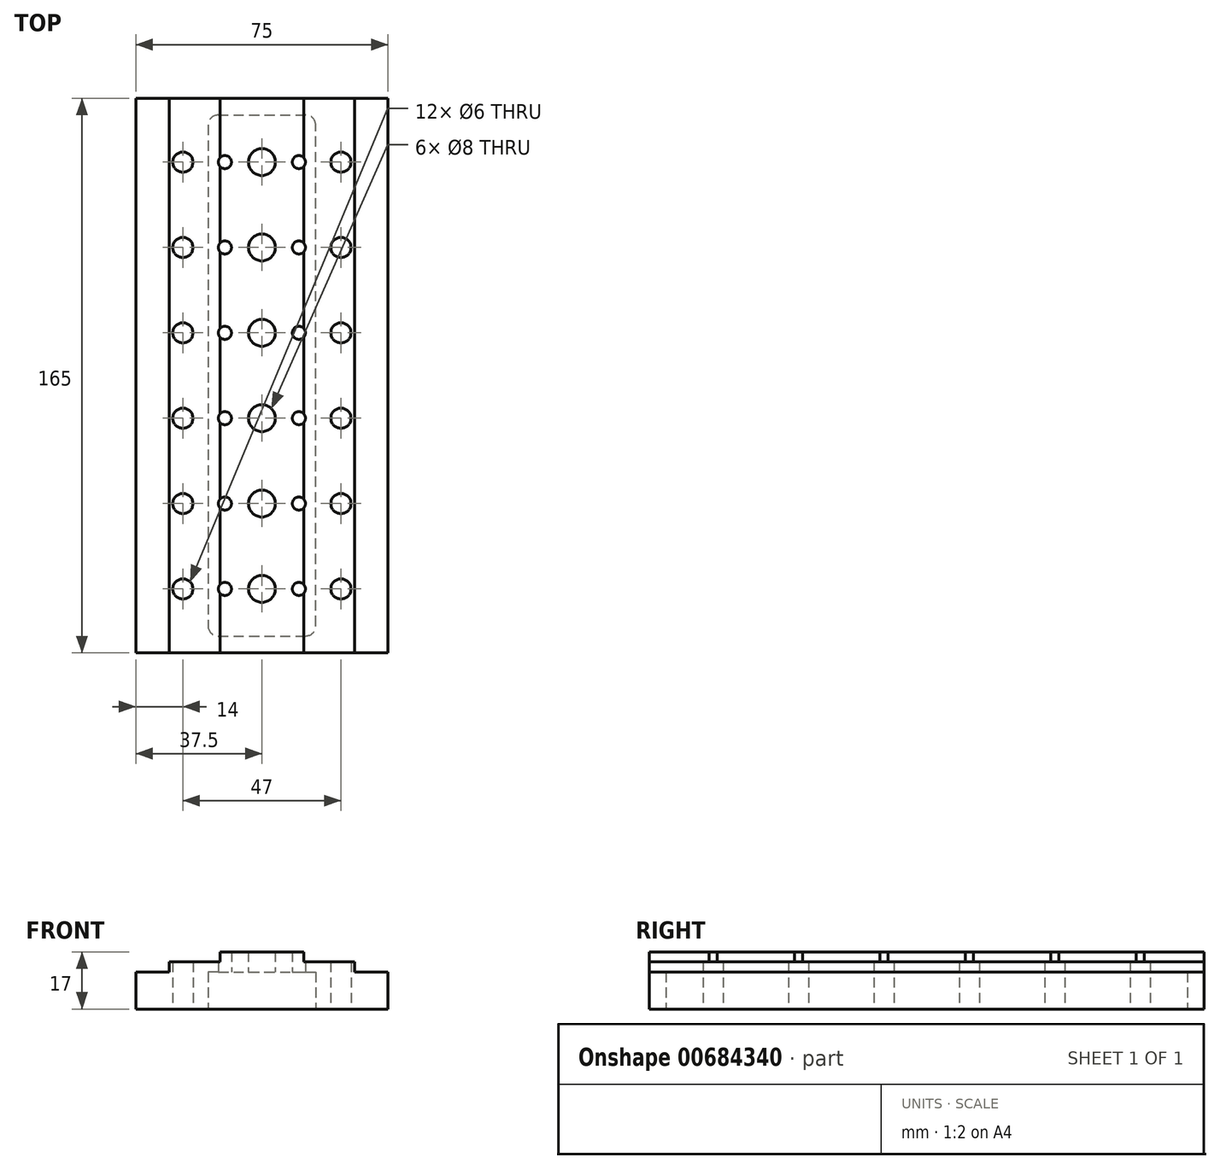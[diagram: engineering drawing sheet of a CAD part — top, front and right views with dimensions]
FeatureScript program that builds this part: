
annotation { "Feature Type Name" : "Feature", "Feature Type Description" : "" }
export const myFeature = defineFeature(function(context is Context, id is Id, definition is map)
    precondition{}
    {
        {
            var Q0;
            Q0=qCreatedBy(makeId("Front.planeOp"),FACE);
            var sketch = newSketch(context, id + "F0", { "sketchPlane" : qUnion([Q0])});
            skLineSegment(sketch, "E0", {"start": v(0, 0) * mm, "end": v(75, 0) * mm});
            skLineSegment(sketch, "E1", {"start": v(75, 14) * mm, "end": v(75, 0) * mm});
            skLineSegment(sketch, "E2", {"start": v(75, 14) * mm, "end": v(50, 14) * mm});
            skLineSegment(sketch, "E3", {"start": v(50, 14) * mm, "end": v(50, 17) * mm});
            skLineSegment(sketch, "E4", {"start": v(50, 17) * mm, "end": v(25, 17) * mm});
            skLineSegment(sketch, "E5", {"start": v(25, 17) * mm, "end": v(25, 14) * mm});
            skLineSegment(sketch, "E6", {"start": v(25, 14) * mm, "end": v(0, 14) * mm});
            skLineSegment(sketch, "E7", {"start": v(0, 14) * mm, "end": v(0, 0) * mm});
            skSolve(sketch);
        }
        {
            var Q0;
            Q0=makeQuery(id+"F0.imprint","IMPRINT",FACE,{"disambiguationData":[TD([[makeQuery(id+"F0.imprint","IMPRINT",EDGE,{"derivedFrom":sQuery(id+"F0.wireOp",EDGE,"E0")}),1.0]])]});
            extrude(context, id + "F1", {"entities" : qUnion([Q0]), "depth" : 165 * mm, "offsetDistance" : 25 * mm});
        }
        {
            var Q0;
            Q0=makeQuery(id+"F1.opExtrude","SWEPT_FACE",FACE,{"disambiguationData":[OSD([sQuery(id+"F0.wireOp",EDGE,"E0")])]});
            var sketch = newSketch(context, id + "F2", { "sketchPlane" : qUnion([Q0])});
            skPoint(sketch, "E8", {"position": v(14, 146) * mm});
            skPoint(sketch, "E9", {"position": v(37.5, 146) * mm});
            skPoint(sketch, "E9.positionSnap0", {"position": v(37.5, 165) * mm});
            skPoint(sketch, "E10", {"position": v(61, 146) * mm});
            skPoint(sketch, "E11", {"position": v(14, 120.6) * mm});
            skPoint(sketch, "E12", {"position": v(14, 95.2) * mm});
            skPoint(sketch, "E13", {"position": v(14, 69.8) * mm});
            skPoint(sketch, "E14", {"position": v(14, 44.4) * mm});
            skPoint(sketch, "E15", {"position": v(14, 19) * mm});
            skPoint(sketch, "E16", {"position": v(37.5, 120.6) * mm});
            skPoint(sketch, "E17", {"position": v(37.5, 95.2) * mm});
            skPoint(sketch, "E18", {"position": v(37.5, 69.8) * mm});
            skPoint(sketch, "E19", {"position": v(37.5, 44.4) * mm});
            skPoint(sketch, "E20", {"position": v(37.5, 19) * mm});
            skPoint(sketch, "E21", {"position": v(61, 120.6) * mm});
            skPoint(sketch, "E22", {"position": v(61, 95.2) * mm});
            skPoint(sketch, "E23", {"position": v(61, 69.8) * mm});
            skPoint(sketch, "E24", {"position": v(61, 44.4) * mm});
            skPoint(sketch, "E25", {"position": v(61, 19) * mm});
            skPoint(sketch, "E26", {"position": v(26.5, 146) * mm});
            skPoint(sketch, "E27", {"position": v(26.5, 120.6) * mm});
            skPoint(sketch, "E28", {"position": v(26.5, 95.2) * mm});
            skPoint(sketch, "E29", {"position": v(26.5, 69.8) * mm});
            skPoint(sketch, "E30", {"position": v(26.5, 44.4) * mm});
            skPoint(sketch, "E31", {"position": v(26.5, 19) * mm});
            skPoint(sketch, "E32", {"position": v(48.5, 146) * mm});
            skPoint(sketch, "E33", {"position": v(48.5, 120.6) * mm});
            skPoint(sketch, "E34", {"position": v(48.5, 95.2) * mm});
            skPoint(sketch, "E35", {"position": v(48.5, 69.8) * mm});
            skPoint(sketch, "E36", {"position": v(48.5, 44.4) * mm});
            skPoint(sketch, "E37", {"position": v(48.5, 19) * mm});
            skSolve(sketch);
        }
        {
            var Q0;
            Q0=sQuery(id+"F2.wireOp",VERTEX,"E8");
            var Q1;
            Q1=sQuery(id+"F2.wireOp",VERTEX,"E11");
            var Q2;
            Q2=sQuery(id+"F2.wireOp",VERTEX,"E12");
            var Q3;
            Q3=sQuery(id+"F2.wireOp",VERTEX,"E13");
            var Q4;
            Q4=sQuery(id+"F2.wireOp",VERTEX,"E14");
            var Q5;
            Q5=sQuery(id+"F2.wireOp",VERTEX,"E15");
            var Q6;
            Q6=sQuery(id+"F2.wireOp",VERTEX,"E10");
            var Q7;
            Q7=sQuery(id+"F2.wireOp",VERTEX,"E21");
            var Q8;
            Q8=sQuery(id+"F2.wireOp",VERTEX,"E22");
            var Q9;
            Q9=sQuery(id+"F2.wireOp",VERTEX,"E23");
            var Q10;
            Q10=sQuery(id+"F2.wireOp",VERTEX,"E24");
            var Q11;
            Q11=sQuery(id+"F2.wireOp",VERTEX,"E25");
            var Q12;
            Q12=makeQuery(id+"F1.opExtrude","SWEPT_BODY",BODY,{"disambiguationData":[OSD([sQuery(id+"F0.wireOp",EDGE,"E0"),sQuery(id+"F0.wireOp",EDGE,"E1"),sQuery(id+"F0.wireOp",EDGE,"E2"),sQuery(id+"F0.wireOp",EDGE,"E3"),sQuery(id+"F0.wireOp",EDGE,"E4"),sQuery(id+"F0.wireOp",EDGE,"E5"),sQuery(id+"F0.wireOp",EDGE,"E6"),sQuery(id+"F0.wireOp",EDGE,"E7")])]});
            hole(context, id + "F3", {"style" : HoleStyle.SIMPLE, "endStyle" : HoleEndStyle.THROUGH, "standardTappedOrClearance" : lookupTablePath({ "standard" : "ISO", "size" : "6", "type" : "Drilled" }), "standardBlindInLast" : lookupTablePath({ "standard" : "ISO", "size" : "6", "type" : "Drilled" }), "holeDiameter" : 6 * mm, "majorDiameter" : 5 * mm, "isTappedThrough" : true, "tappedDepth" : 17.25 * mm, "tapClearance" : 3, "startFromSketch" : true, "locations" : qUnion([Q0, Q1, Q2, Q3, Q4, Q5, Q6, Q7, Q8, Q9, Q10, Q11]), "scope" : qUnion([Q12])});
        }
        {
            var Q0;
            Q0=sQuery(id+"F2.wireOp",VERTEX,"E26");
            var Q1;
            Q1=sQuery(id+"F2.wireOp",VERTEX,"E27");
            var Q2;
            Q2=sQuery(id+"F2.wireOp",VERTEX,"E28");
            var Q3;
            Q3=sQuery(id+"F2.wireOp",VERTEX,"E29");
            var Q4;
            Q4=sQuery(id+"F2.wireOp",VERTEX,"E30");
            var Q5;
            Q5=sQuery(id+"F2.wireOp",VERTEX,"E31");
            var Q6;
            Q6=sQuery(id+"F2.wireOp",VERTEX,"E37");
            var Q7;
            Q7=sQuery(id+"F2.wireOp",VERTEX,"E36");
            var Q8;
            Q8=sQuery(id+"F2.wireOp",VERTEX,"E35");
            var Q9;
            Q9=sQuery(id+"F2.wireOp",VERTEX,"E34");
            var Q10;
            Q10=sQuery(id+"F2.wireOp",VERTEX,"E33");
            var Q11;
            Q11=sQuery(id+"F2.wireOp",VERTEX,"E32");
            var Q12;
            Q12=makeQuery(id+"F1.opExtrude","SWEPT_BODY",BODY,{"disambiguationData":[OSD([sQuery(id+"F0.wireOp",EDGE,"E0"),sQuery(id+"F0.wireOp",EDGE,"E1"),sQuery(id+"F0.wireOp",EDGE,"E2"),sQuery(id+"F0.wireOp",EDGE,"E3"),sQuery(id+"F0.wireOp",EDGE,"E4"),sQuery(id+"F0.wireOp",EDGE,"E5"),sQuery(id+"F0.wireOp",EDGE,"E6"),sQuery(id+"F0.wireOp",EDGE,"E7")])]});
            hole(context, id + "F4", {"style" : HoleStyle.SIMPLE, "endStyle" : HoleEndStyle.THROUGH, "standardTappedOrClearance" : lookupTablePath({ "standard" : "ISO", "size" : "3.9", "type" : "Drilled" }), "standardBlindInLast" : lookupTablePath({ "standard" : "ISO", "size" : "3.9", "type" : "Drilled" }), "holeDiameter" : 3.9 * mm, "majorDiameter" : 5 * mm, "isTappedThrough" : true, "tappedDepth" : 17.25 * mm, "tapClearance" : 3, "startFromSketch" : true, "locations" : qUnion([Q0, Q1, Q2, Q3, Q4, Q5, Q6, Q7, Q8, Q9, Q10, Q11]), "scope" : qUnion([Q12])});
        }
        {
            var Q0;
            Q0=sQuery(id+"F2.wireOp",VERTEX,"E9");
            var Q1;
            Q1=sQuery(id+"F2.wireOp",VERTEX,"E16");
            var Q2;
            Q2=sQuery(id+"F2.wireOp",VERTEX,"E17");
            var Q3;
            Q3=sQuery(id+"F2.wireOp",VERTEX,"E18");
            var Q4;
            Q4=sQuery(id+"F2.wireOp",VERTEX,"E19");
            var Q5;
            Q5=sQuery(id+"F2.wireOp",VERTEX,"E20");
            var Q6;
            Q6=makeQuery(id+"F1.opExtrude","SWEPT_BODY",BODY,{"disambiguationData":[OSD([sQuery(id+"F0.wireOp",EDGE,"E0"),sQuery(id+"F0.wireOp",EDGE,"E1"),sQuery(id+"F0.wireOp",EDGE,"E2"),sQuery(id+"F0.wireOp",EDGE,"E3"),sQuery(id+"F0.wireOp",EDGE,"E4"),sQuery(id+"F0.wireOp",EDGE,"E5"),sQuery(id+"F0.wireOp",EDGE,"E6"),sQuery(id+"F0.wireOp",EDGE,"E7")])]});
            hole(context, id + "F5", {"style" : HoleStyle.SIMPLE, "endStyle" : HoleEndStyle.THROUGH, "standardTappedOrClearance" : lookupTablePath({ "standard" : "ISO", "size" : "8", "type" : "Drilled" }), "standardBlindInLast" : lookupTablePath({ "standard" : "ISO", "size" : "8", "type" : "Drilled" }), "holeDiameter" : 8 * mm, "majorDiameter" : 5 * mm, "isTappedThrough" : true, "tappedDepth" : 17.25 * mm, "tapClearance" : 3, "startFromSketch" : true, "locations" : qUnion([Q0, Q1, Q2, Q3, Q4, Q5]), "scope" : qUnion([Q6])});
        }
        {
            var Q0;
            {var subQ0=sQuery(id+"F0.wireOp",EDGE,"E0");Q0=makeQuery(id+"F2.imprint","IMPRINT",FACE,{"disambiguationData":[TD([[makeQuery(id+"F2.imprint","IMPRINT",EDGE,{"derivedFrom":makeQuery(id+"F1.opExtrude","CAP_EDGE",EDGE,{"disambiguationData":[OSD([subQ0])],"isStart":true})}),1.0]])]});}
            var sketch = newSketch(context, id + "F6", { "sketchPlane" : qUnion([Q0])});
            skLineSegment(sketch, "E38", {"start": v(21.5, 160) * mm, "end": v(53.5, 160) * mm});
            skLineSegment(sketch, "E39", {"start": v(53.5, 160) * mm, "end": v(53.5, 5) * mm});
            skLineSegment(sketch, "E40", {"start": v(21.5, 5) * mm, "end": v(53.5, 5) * mm});
            skLineSegment(sketch, "E41", {"start": v(21.5, 5) * mm, "end": v(21.5, 160) * mm});
            skSolve(sketch);
        }
        {
            var Q0;
            Q0=makeQuery(id+"F6.imprint","IMPRINT",FACE,{"disambiguationData":[TD([[makeQuery(id+"F6.imprint","IMPRINT",EDGE,{"derivedFrom":sQuery(id+"F6.wireOp",EDGE,"E38")}),-1.0]])]});
            extrude(context, id + "F7", {"entities" : qUnion([Q0]), "operationType" : NewBodyOperationType.REMOVE, "oppositeDirection" : true, "depth" : 11 * mm, "offsetDistance" : 25 * mm});
        }
        {
            var Q0;
            Q0=makeQuery(id+"F7.boolean.opBoolean","COPY",EDGE,{"derivedFrom":makeQuery(id+"F7.opExtrude","SWEPT_EDGE",EDGE,{"disambiguationData":[OSD([sQuery(id+"F6.wireOp",EDGE,"E38"),sQuery(id+"F6.wireOp",EDGE,"E41")])]})});
            var Q1;
            Q1=makeQuery(id+"F7.boolean.opBoolean","COPY",EDGE,{"derivedFrom":makeQuery(id+"F7.opExtrude","SWEPT_EDGE",EDGE,{"disambiguationData":[OSD([sQuery(id+"F6.wireOp",EDGE,"E38"),sQuery(id+"F6.wireOp",EDGE,"E39")])]})});
            var Q2;
            Q2=makeQuery(id+"F7.boolean.opBoolean","COPY",EDGE,{"derivedFrom":makeQuery(id+"F7.opExtrude","SWEPT_EDGE",EDGE,{"disambiguationData":[OSD([sQuery(id+"F6.wireOp",EDGE,"E40"),sQuery(id+"F6.wireOp",EDGE,"E41")])]})});
            var Q3;
            Q3=makeQuery(id+"F7.boolean.opBoolean","COPY",EDGE,{"derivedFrom":makeQuery(id+"F7.opExtrude","SWEPT_EDGE",EDGE,{"disambiguationData":[OSD([sQuery(id+"F6.wireOp",EDGE,"E39"),sQuery(id+"F6.wireOp",EDGE,"E40")])]})});
            fillet(context, id + "F8", {"entities" : qUnion([Q0, Q1, Q2, Q3]), "radius" : 3 * mm, "tangentPropagation" : true, "allowEdgeOverflow" : false});
        }
        {
            var Q0;
            Q0=makeQuery(id+"F1.opExtrude","SWEPT_FACE",FACE,{"disambiguationData":[OSD([sQuery(id+"F0.wireOp",EDGE,"E2")])]});
            var sketch = newSketch(context, id + "F9", { "sketchPlane" : qUnion([Q0])});
            skLineSegment(sketch, "E42", {"start": v(65, 0) * mm, "end": v(65, -165) * mm});
            skLineSegment(sketch, "E43", {"start": v(65, -165) * mm, "end": v(75, -165) * mm});
            skLineSegment(sketch, "E44", {"start": v(75, -165) * mm, "end": v(75, 0) * mm});
            skLineSegment(sketch, "E45", {"start": v(75, 0) * mm, "end": v(65, 0) * mm});
            skSolve(sketch);
        }
        {
            var Q0;
            Q0=makeQuery(id+"F1.opExtrude","SWEPT_FACE",FACE,{"disambiguationData":[OSD([sQuery(id+"F0.wireOp",EDGE,"E6")])]});
            var sketch = newSketch(context, id + "F10", { "sketchPlane" : qUnion([Q0])});
            skLineSegment(sketch, "E46", {"start": v(10, 0) * mm, "end": v(10, -165) * mm});
            skLineSegment(sketch, "E47", {"start": v(10, -165) * mm, "end": v(0, -165) * mm});
            skLineSegment(sketch, "E48", {"start": v(0, -165) * mm, "end": v(0, 0) * mm});
            skLineSegment(sketch, "E49", {"start": v(0, 0) * mm, "end": v(10, 0) * mm});
            skSolve(sketch);
        }
        {
            var Q0;
            Q0=makeQuery(id+"F10.imprint","IMPRINT",FACE,{"disambiguationData":[TD([[makeQuery(id+"F10.imprint","IMPRINT",EDGE,{"derivedFrom":sQuery(id+"F10.wireOp",EDGE,"E46")}),-1.0]])]});
            extrude(context, id + "F11", {"entities" : qUnion([Q0]), "operationType" : NewBodyOperationType.REMOVE, "oppositeDirection" : true, "depth" : 3 * mm, "offsetDistance" : 25 * mm});
        }
        {
            var Q0;
            Q0=makeQuery(id+"F9.imprint","IMPRINT",FACE,{"disambiguationData":[TD([[makeQuery(id+"F9.imprint","IMPRINT",EDGE,{"derivedFrom":sQuery(id+"F9.wireOp",EDGE,"E42")}),1.0]])]});
            extrude(context, id + "F12", {"entities" : qUnion([Q0]), "operationType" : NewBodyOperationType.REMOVE, "oppositeDirection" : true, "depth" : 3 * mm, "offsetDistance" : 25 * mm});
        }
    });
